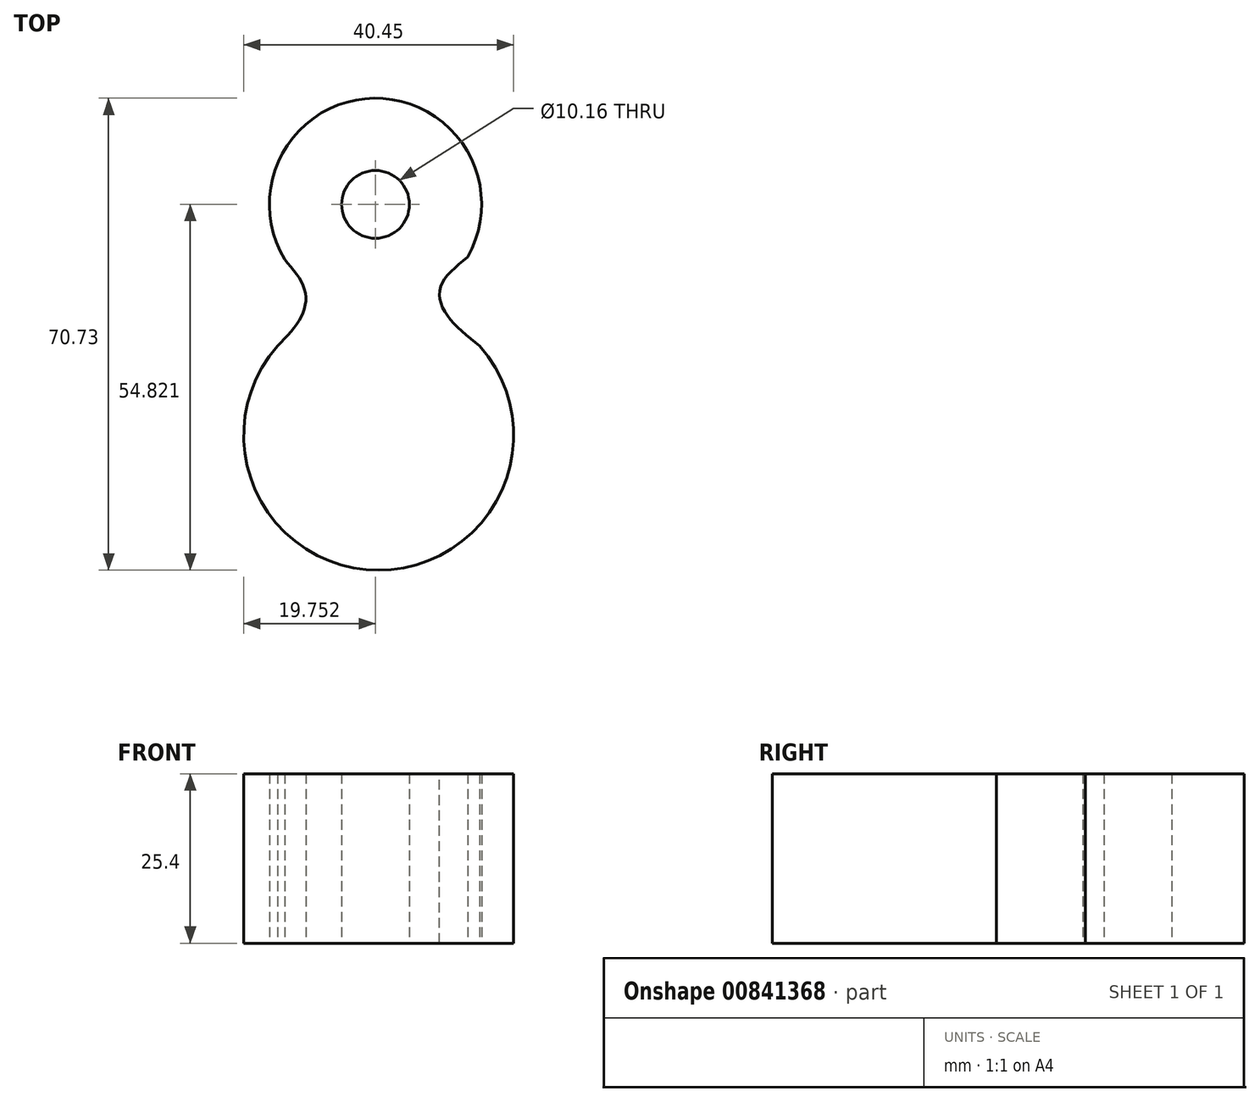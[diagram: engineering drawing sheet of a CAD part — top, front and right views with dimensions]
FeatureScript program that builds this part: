
annotation { "Feature Type Name" : "Feature", "Feature Type Description" : "" }
export const myFeature = defineFeature(function(context is Context, id is Id, definition is map)
    precondition{}
    {
        {
            var Q0;
            Q0=qCreatedBy(makeId("Top.planeOp"),FACE);
            var sketch = newSketch(context, id + "F0", { "sketchPlane" : qUnion([Q0])});
            skArc(sketch, "E0", {"start": v(-14.8, 0) * mm, "mid": v(0.37, -33.6) * mm, "end": v(15.54, 0) * mm});
            skArc(sketch, "E1", {"start": v(13.71, 13.34) * mm, "mid": v(-0.32, 37.14) * mm, "end": v(-13.71, 12.98) * mm});
            skFitSpline(sketch, "E2", {"points": [v(-13.71, 12.98) * mm, v(-10.79, 8.6) * mm, v(-11.15, 4.57) * mm, v(-14.8, 0) * mm], "startDerivative": vector(10.75, -12.63) * mm, "endDerivative": vector(-12.08, -12.45) * mm});
            skFitSpline(sketch, "E3", {"points": [v(13.71, 13.34) * mm, v(9.69, 8.96) * mm, v(10.42, 4.94) * mm, v(15.54, 0) * mm], "startDerivative": vector(-15.18, -12.37) * mm, "endDerivative": vector(16.03, -12.8) * mm});
            skSolve(sketch);
        }
        {
            var Q0;
            Q0=makeQuery(id+"F0.imprint","IMPRINT",FACE,{"disambiguationData":[TD([[makeQuery(id+"F0.imprint","IMPRINT",EDGE,{"derivedFrom":sQuery(id+"F0.wireOp",EDGE,"E0")}),1.0]])]});
            extrude(context, id + "F1", {"entities" : qUnion([Q0]), "depth" : 25.4 * mm, "offsetDistance" : 25.4 * mm});
        }
        {
            var Q0;
            Q0=sQuery(id+"F0.wireOp",VERTEX,"E1.center");
            var Q1;
            Q1=makeQuery(id+"F1.opExtrude","SWEPT_BODY",BODY,{"disambiguationData":[OSD([sQuery(id+"F0.wireOp",EDGE,"E0"),sQuery(id+"F0.wireOp",EDGE,"E1"),sQuery(id+"F0.wireOp",EDGE,"E2"),sQuery(id+"F0.wireOp",EDGE,"E3")])]});
            hole(context, id + "F2", {"style" : HoleStyle.SIMPLE, "endStyle" : HoleEndStyle.THROUGH, "oppositeDirection" : true, "holeDiameter" : 10.16 * mm, "majorDiameter" : 6.35 * mm, "isTappedThrough" : true, "tappedDepth" : 12.7 * mm, "tapClearance" : 3, "locations" : qUnion([Q0]), "scope" : qUnion([Q1])});
        }
    });
